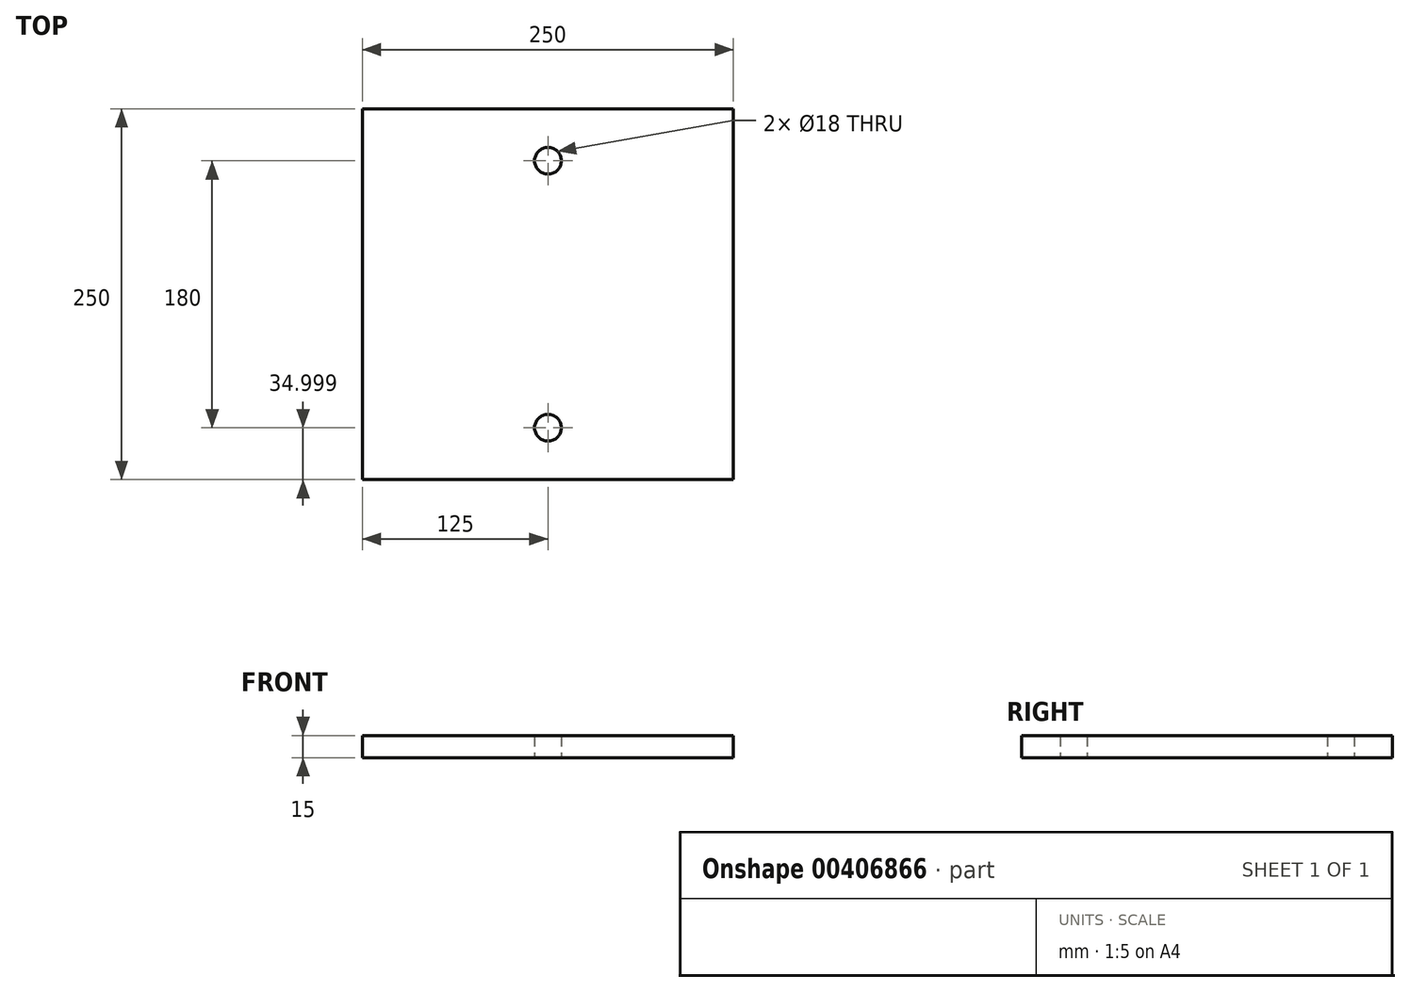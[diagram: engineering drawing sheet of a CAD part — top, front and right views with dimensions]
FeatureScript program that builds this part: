
annotation { "Feature Type Name" : "Feature", "Feature Type Description" : "" }
export const myFeature = defineFeature(function(context is Context, id is Id, definition is map)
    precondition{}
    {
        {
            var Q0;
            Q0=qCreatedBy(makeId("Top.planeOp"),FACE);
            var sketch = newSketch(context, id + "F0", { "sketchPlane" : qUnion([Q0])});
            skLineSegment(sketch, "E0.bottom", {"start": v(-125, 81.36) * mm, "end": v(125, 81.36) * mm});
            skLineSegment(sketch, "E0.top", {"start": v(-125, -168.64) * mm, "end": v(125, -168.64) * mm});
            skLineSegment(sketch, "E0.left", {"start": v(-125, 81.36) * mm, "end": v(-125, -168.64) * mm});
            skLineSegment(sketch, "E0.right", {"start": v(125, 81.36) * mm, "end": v(125, -168.64) * mm});
            skCircle(sketch, "E1", {"center": v(0, 46.36) * mm, "radius": 9 * mm});
            skCircle(sketch, "E2", {"center": v(0, -133.64) * mm, "radius": 9 * mm});
            skLineSegment(sketch, "E3.bottom", {"start": v(-43.4, -13.64) * mm, "end": v(56.6, -13.64) * mm, "construction": true});
            skLineSegment(sketch, "E3.top", {"start": v(-43.4, -73.64) * mm, "end": v(56.6, -73.64) * mm, "construction": true});
            skLineSegment(sketch, "E3.left", {"start": v(-43.4, -13.64) * mm, "end": v(-43.4, -73.64) * mm, "construction": true});
            skLineSegment(sketch, "E3.right", {"start": v(56.6, -13.64) * mm, "end": v(56.6, -73.64) * mm, "construction": true});
            skSolve(sketch);
        }
        {
            var Q0;
            Q0 = qSketchRegion(id + "F0", true);
            extrude(context, id + "F1", {"entities" : qUnion([Q0]), "depth" : 15 * mm});
        }
    });
